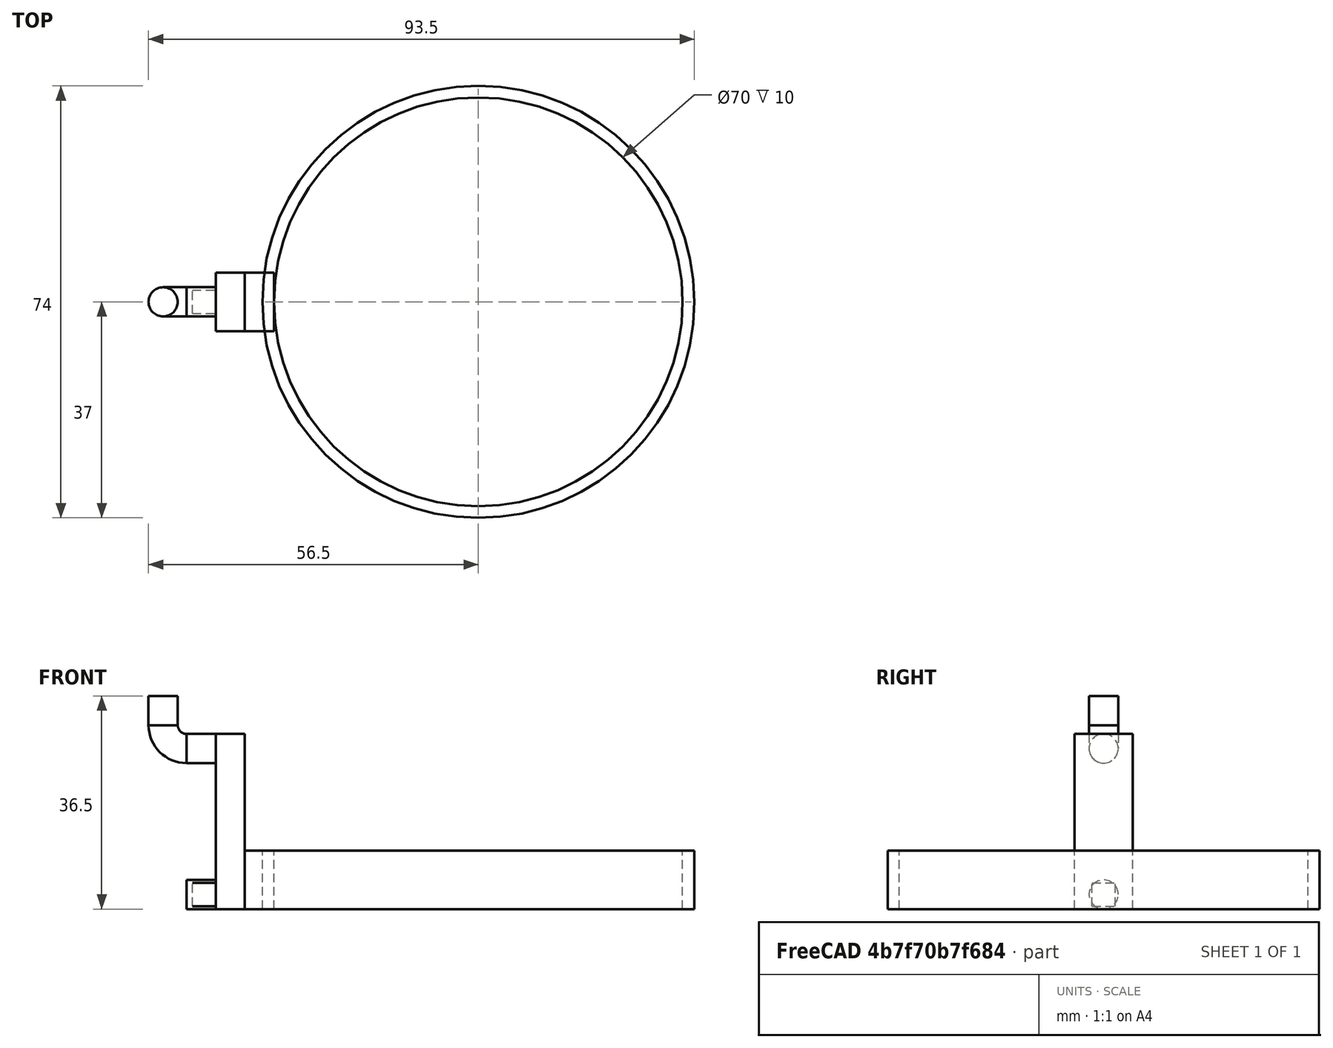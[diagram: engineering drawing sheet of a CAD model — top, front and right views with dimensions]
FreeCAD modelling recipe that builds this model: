
FCSTD DOCUMENT  (FreeCAD 0.17R13522 (Git))
Label: cupholder
License: All rights reserved
LicenseURL: http://en.wikipedia.org/wiki/All_rights_reserved
objects: Part::Cylinder×5, Part::Box×3, Part::Torus×1, Part::Cut×1
note: 10 computed .brp shape members not serialized (recipe doc carries the construction recipe); baked Part::Feature solids carry a one-line shape summary decoded from their .brp

FEATURE [Part::Cylinder] Cylinder
  Angle = 360
  AttacherType = Attacher::AttachEngine3D
  Height = 10
  Placement = pos=(35,0,0) rot=(0,0,1;0rad)
  Radius = 37
FEATURE [Part::Box] Box  label="Cube"
  AttacherType = Attacher::AttachEngine3D
  Height = 10
  Length = 5
  Placement = pos=(-5,-5,0) rot=(0,0,1;0rad)
  Width = 10
FEATURE [Part::Box] Box001  label="Cube001"
  AttacherType = Attacher::AttachEngine3D
  Height = 30
  Length = 5
  Placement = pos=(-10,-5,0) rot=(0,0,1;0rad)
  Width = 10
FEATURE [Part::Cylinder] Cylinder002
  Angle = 360
  AttacherType = Attacher::AttachEngine3D
  Height = 5
  Placement = pos=(-10,0,2.5) rot=(0,-1,0;1.5708rad)
  Radius = 2.5
FEATURE [Part::Cylinder] Cylinder003
  Angle = 360
  AttacherType = Attacher::AttachEngine3D
  Height = 5
  Placement = pos=(-10,0,27.5) rot=(0,-1,0;1.5708rad)
  Radius = 2.5
FEATURE [Part::Torus] Torus
  Angle1 = -180
  Angle2 = 180
  Angle3 = 90
  AttacherType = Attacher::AttachEngine3D
  Placement = pos=(-15,0,31.5) rot=(0.57735,-0.57735,-0.57735;4.18879rad)
  Radius1 = 4
  Radius2 = 2.5
FEATURE [Part::Cylinder] Cylinder004
  Angle = 360
  AttacherType = Attacher::AttachEngine3D
  Height = 5
  Placement = pos=(-19,0,31.5) rot=(0,0,1;0rad)
  Radius = 2.5
FEATURE [Part::Box] Box002  label="Cube002"
  AttacherType = Attacher::AttachEngine3D
  Height = 4
  Length = 4
  Placement = pos=(-14,-2,0.5) rot=(0,0,1;0rad)
  Width = 4
FEATURE [Part::Cylinder] Cylinder005
  Angle = 360
  AttacherType = Attacher::AttachEngine3D
  Height = 10
  Placement = pos=(35,0,0) rot=(0,0,1;0rad)
  Radius = 35
FEATURE [Part::Cut] Cut
  Base = -> Cylinder
  Tool = -> Cylinder005
